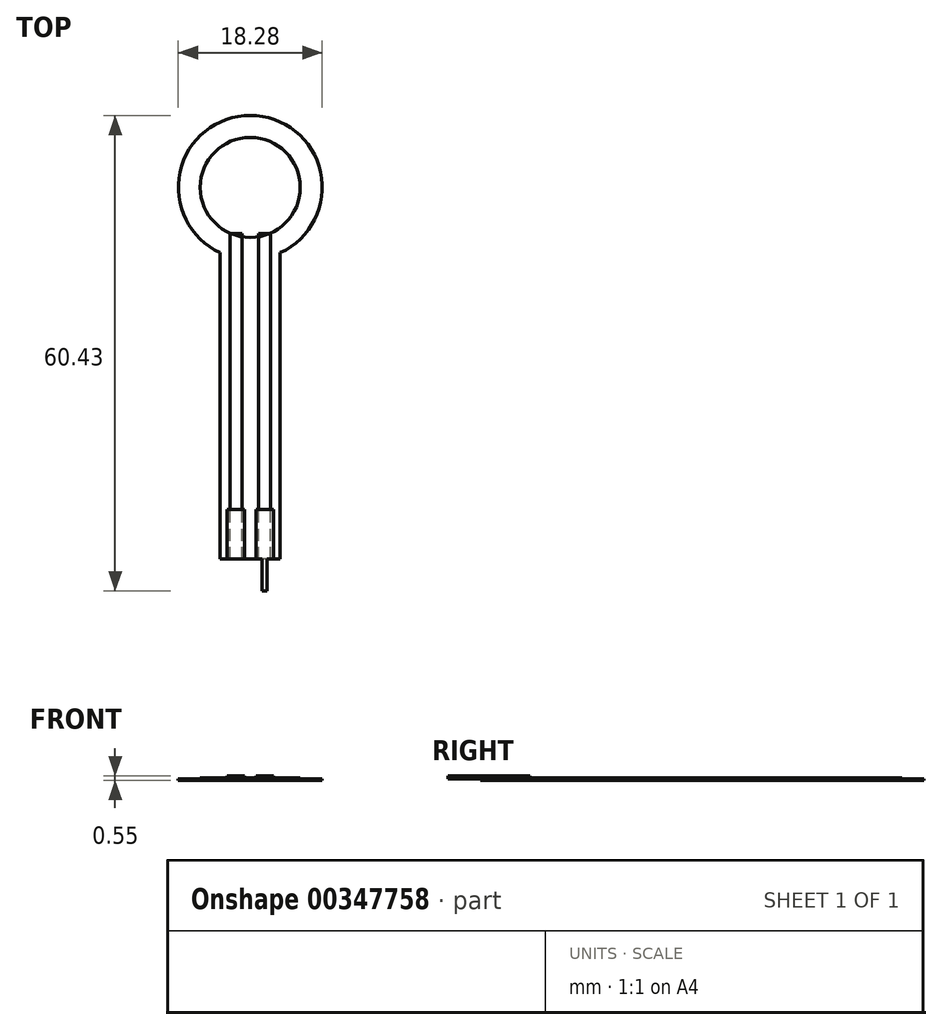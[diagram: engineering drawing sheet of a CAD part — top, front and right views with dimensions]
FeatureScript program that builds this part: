
annotation { "Feature Type Name" : "Feature", "Feature Type Description" : "" }
export const myFeature = defineFeature(function(context is Context, id is Id, definition is map)
    precondition{}
    {
        {
            var Q0;
            Q0=qCreatedBy(makeId("Top.planeOp"),FACE);
            var sketch = newSketch(context, id + "F0", { "sketchPlane" : qUnion([Q0])});
            skCircle(sketch, "E0", {"center": v(0, 0) * mm, "radius": 9.14 * mm});
            skCircle(sketch, "E1", {"center": v(0, 0) * mm, "radius": 6.35 * mm});
            skLineSegment(sketch, "E2", {"start": v(0, 0) * mm, "end": v(0, -47.19) * mm, "construction": true});
            skLineSegment(sketch, "E3.bottom", {"start": v(3.81, -47.19) * mm, "end": v(-3.81, -47.19) * mm});
            skLineSegment(sketch, "E3.left", {"start": v(3.81, -47.19) * mm, "end": v(3.81, -8.3) * mm});
            skLineSegment(sketch, "E3.right", {"start": v(-3.81, -47.19) * mm, "end": v(-3.81, -8.3) * mm});
            skPoint(sketch, "E3.middle", {"position": v(0, -23.6) * mm});
            skSolve(sketch);
        }
        {
            var Q0;
            Q0=makeQuery(id+"F0.imprint","IMPRINT",FACE,{"disambiguationData":[TD([[makeQuery(id+"F0.imprint","IMPRINT",EDGE,{"derivedFrom":sQuery(id+"F0.wireOp",EDGE,"E3.bottom")}),-1.0]])]});
            var Q1;
            Q1=makeQuery(id+"F0.imprint","IMPRINT",FACE,{"disambiguationData":[TD([[makeQuery(id+"F0.imprint","IMPRINT",EDGE,{"derivedFrom":sQuery(id+"F0.wireOp",EDGE,"E1")}),-1.0]])]});
            var Q2;
            Q2=makeQuery(id+"F0.imprint","IMPRINT",FACE,{"disambiguationData":[TD([[makeQuery(id+"F0.imprint","IMPRINT",EDGE,{"derivedFrom":sQuery(id+"F0.wireOp",EDGE,"E1")}),1.0]])]});
            extrude(context, id + "F1", {"entities" : qUnion([Q0, Q1, Q2]), "depth" : .2 * mm});
        }
        {
            var Q0;
            Q0=makeQuery(id+"F0.imprint","IMPRINT",FACE,{"disambiguationData":[TD([[makeQuery(id+"F0.imprint","IMPRINT",EDGE,{"derivedFrom":sQuery(id+"F0.wireOp",EDGE,"E1")}),1.0]])]});
            extrude(context, id + "F2", {"entities" : qUnion([Q0]), "depth" : .3 * mm});
        }
        {
            var Q0;
            Q0=makeQuery(id+"F1.opExtrude","CAP_FACE",FACE,{"disambiguationData":[OSD([sQuery(id+"F0.wireOp",EDGE,"E0"),sQuery(id+"F0.wireOp",EDGE,"E3.bottom"),sQuery(id+"F0.wireOp",EDGE,"E3.left"),sQuery(id+"F0.wireOp",EDGE,"E3.right")])],"isStart":false});
            var sketch = newSketch(context, id + "F3", { "sketchPlane" : qUnion([Q0])});
            skLineSegment(sketch, "E4.bottom", {"start": v(-2.56, -47.19) * mm, "end": v(-1.05, -47.19) * mm});
            skLineSegment(sketch, "E4.top", {"start": v(-2.56, -5.89) * mm, "end": v(-1.05, -5.89) * mm});
            skLineSegment(sketch, "E4.left", {"start": v(-2.56, -47.19) * mm, "end": v(-2.56, -5.89) * mm});
            skLineSegment(sketch, "E4.right", {"start": v(-1.05, -47.19) * mm, "end": v(-1.05, -5.89) * mm});
            skLineSegment(sketch, "E5.MirrorCS", {"start": v(2.56, -47.19) * mm, "end": v(1.05, -47.19) * mm});
            skLineSegment(sketch, "E6.MirrorCS", {"start": v(1.05, -47.19) * mm, "end": v(1.05, -5.89) * mm});
            skLineSegment(sketch, "E7.MirrorCS", {"start": v(2.56, -47.19) * mm, "end": v(2.56, -5.89) * mm});
            skLineSegment(sketch, "E8.MirrorCS", {"start": v(2.56, -5.89) * mm, "end": v(1.05, -5.89) * mm});
            skSolve(sketch);
        }
        {
            var Q0;
            Q0=makeQuery(id+"F3.imprint","IMPRINT",FACE,{"disambiguationData":[TD([[makeQuery(id+"F3.imprint","IMPRINT",EDGE,{"derivedFrom":sQuery(id+"F3.wireOp",EDGE,"E4.bottom")}),-1.0]])]});
            var Q1;
            Q1=makeQuery(id+"F3.imprint","IMPRINT",FACE,{"disambiguationData":[TD([[makeQuery(id+"F3.imprint","IMPRINT",EDGE,{"derivedFrom":sQuery(id+"F3.wireOp",EDGE,"E5.MirrorCS")}),-1.0]])]});
            extrude(context, id + "F4", {"entities" : qUnion([Q0, Q1]), "depth" : .1 * mm});
        }
        {
            var Q0;
            Q0=makeQuery(id+"F1.opExtrude","CAP_FACE",FACE,{"disambiguationData":[OSD([sQuery(id+"F0.wireOp",EDGE,"E0"),sQuery(id+"F0.wireOp",EDGE,"E3.bottom"),sQuery(id+"F0.wireOp",EDGE,"E3.left"),sQuery(id+"F0.wireOp",EDGE,"E3.right")])],"isStart":false});
            var sketch = newSketch(context, id + "F5", { "sketchPlane" : qUnion([Q0])});
            skLineSegment(sketch, "E9.bottom", {"start": v(-2.95, -47.19) * mm, "end": v(-0.7, -47.19) * mm});
            skLineSegment(sketch, "E9.top", {"start": v(-2.95, -40.92) * mm, "end": v(-0.7, -40.92) * mm});
            skLineSegment(sketch, "E9.left", {"start": v(-2.95, -47.19) * mm, "end": v(-2.95, -40.92) * mm});
            skLineSegment(sketch, "E9.right", {"start": v(-0.7, -47.19) * mm, "end": v(-0.7, -40.92) * mm});
            skLineSegment(sketch, "E10.MirrorCS", {"start": v(2.95, -47.19) * mm, "end": v(0.7, -47.19) * mm});
            skLineSegment(sketch, "E11.MirrorCS", {"start": v(0.7, -47.19) * mm, "end": v(0.7, -40.92) * mm});
            skLineSegment(sketch, "E12.MirrorCS", {"start": v(2.95, -47.19) * mm, "end": v(2.95, -40.92) * mm});
            skLineSegment(sketch, "E13.MirrorCS", {"start": v(2.95, -40.92) * mm, "end": v(0.7, -40.92) * mm});
            skLineSegment(sketch, "E14.bottom", {"start": v(-2.14, -47.19) * mm, "end": v(-1.48, -47.19) * mm});
            skLineSegment(sketch, "E14.top", {"start": v(-2.14, -51.29) * mm, "end": v(-1.48, -51.29) * mm});
            skLineSegment(sketch, "E14.left", {"start": v(-2.14, -47.19) * mm, "end": v(-2.14, -51.29) * mm});
            skLineSegment(sketch, "E14.right", {"start": v(-1.48, -47.19) * mm, "end": v(-1.48, -51.29) * mm});
            skLineSegment(sketch, "E15.MirrorCS", {"start": v(2.14, -51.29) * mm, "end": v(1.48, -51.29) * mm});
            skLineSegment(sketch, "E16.MirrorCS", {"start": v(2.14, -47.19) * mm, "end": v(2.14, -51.29) * mm});
            skLineSegment(sketch, "E17.MirrorCS", {"start": v(1.48, -47.19) * mm, "end": v(1.48, -51.29) * mm});
            skSolve(sketch);
        }
        {
            var Q0;
            Q0=makeQuery(id+"F5.imprint","IMPRINT",FACE,{"disambiguationData":[TD([[makeQuery(id+"F5.imprint","IMPRINT",EDGE,{"derivedFrom":sQuery(id+"F5.wireOp",EDGE,"E9.bottom")}),-1.0]])]});
            var Q1;
            Q1=makeQuery(id+"F5.imprint","IMPRINT",FACE,{"disambiguationData":[TD([[makeQuery(id+"F5.imprint","IMPRINT",EDGE,{"derivedFrom":sQuery(id+"F5.wireOp",EDGE,"E10.MirrorCS")}),-1.0]])]});
            var Q2;
            Q2=makeQuery(id+"F5.imprint","IMPRINT",FACE,{"disambiguationData":[TD([[makeQuery(id+"F5.imprint","IMPRINT",EDGE,{"derivedFrom":sQuery(id+"F5.wireOp",EDGE,"E14.bottom")}),1.0]])]});
            var Q3;
            Q3=makeQuery(id+"F5.imprint","IMPRINT",FACE,{"disambiguationData":[TD([[makeQuery(id+"F5.imprint","IMPRINT",EDGE,{"derivedFrom":sQuery(id+"F5.wireOp",EDGE,"E15.MirrorCS")}),-1.0]])]});
            extrude(context, id + "F6", {"entities" : qUnion([Q0, Q1, Q2, Q3]), "depth" : .35 * mm});
        }
    });
